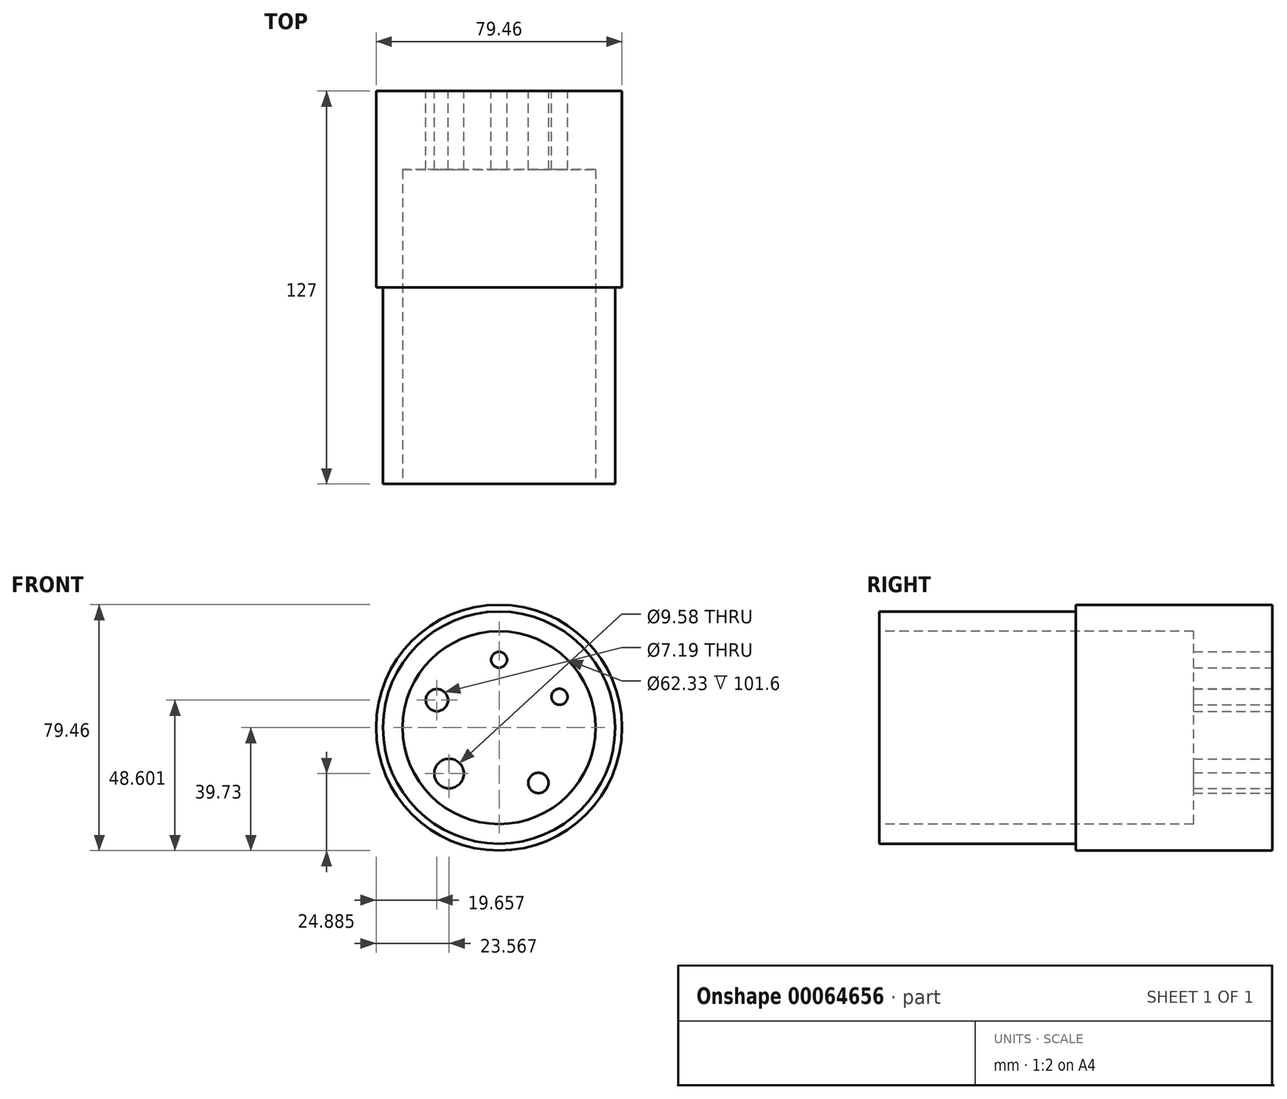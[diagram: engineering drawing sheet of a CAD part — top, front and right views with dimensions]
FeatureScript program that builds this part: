
annotation { "Feature Type Name" : "Feature", "Feature Type Description" : "" }
export const myFeature = defineFeature(function(context is Context, id is Id, definition is map)
    precondition{}
    {
        {
            var Q0;
            Q0=qCreatedBy(makeId("Front.planeOp"),FACE);
            var sketch = newSketch(context, id + "F0", { "sketchPlane" : qUnion([Q0])});
            skCircle(sketch, "E0", {"center": v(0, 0) * mm, "radius": 37.52 * mm});
            skSolve(sketch);
        }
        {
            var Q0;
            Q0=qCreatedBy(makeId("Front.planeOp"),FACE);
            var sketch = newSketch(context, id + "F1", { "sketchPlane" : qUnion([Q0])});
            skCircle(sketch, "E1", {"center": v(0, 0) * mm, "radius": 39.73 * mm});
            skSolve(sketch);
        }
        {
            var Q0;
            Q0=makeQuery(id+"F0.imprint","IMPRINT",FACE,{"disambiguationData":[TD([[makeQuery(id+"F0.imprint","IMPRINT",EDGE,{"derivedFrom":sQuery(id+"F0.wireOp",EDGE,"E0")}),1.0]])]});
            extrude(context, id + "F2", {"entities" : qUnion([Q0]), "depth" : 63.5 * mm});
        }
        {
            var Q0;
            Q0=makeQuery(id+"F1.imprint","IMPRINT",FACE,{"disambiguationData":[TD([[makeQuery(id+"F1.imprint","IMPRINT",EDGE,{"derivedFrom":sQuery(id+"F1.wireOp",EDGE,"E1")}),1.0]])]});
            extrude(context, id + "F3", {"entities" : qUnion([Q0]), "operationType" : NewBodyOperationType.ADD, "oppositeDirection" : true, "depth" : 63.5 * mm});
        }
        {
            var Q0;
            Q0=makeQuery(id+"F3.opExtrude","CAP_FACE",FACE,{"disambiguationData":[OSD([sQuery(id+"F1.wireOp",EDGE,"E1")])],"isStart":false});
            var sketch = newSketch(context, id + "F4", { "sketchPlane" : qUnion([Q0])});
            skCircle(sketch, "E2", {"center": v(0, 21.95) * mm, "radius": 2.57 * mm});
            skCircle(sketch, "E3", {"center": v(-19.55, 9.98) * mm, "radius": 2.6 * mm});
            skCircle(sketch, "E4", {"center": v(20.07, 8.87) * mm, "radius": 3.6 * mm});
            skCircle(sketch, "E5", {"center": v(-12.72, -17.88) * mm, "radius": 3.28 * mm});
            skCircle(sketch, "E6", {"center": v(16.16, -14.85) * mm, "radius": 4.79 * mm});
            skSolve(sketch);
        }
        {
            var Q0;
            Q0 = qSketchRegion(id + "F4", true);
            extrude(context, id + "F5", {"entities" : qUnion([Q0]), "operationType" : NewBodyOperationType.REMOVE, "endBound" : BoundingType.THROUGH_ALL, "oppositeDirection" : true, "depth" : 25.4 * mm});
        }
        {
            var Q0;
            Q0=makeQuery(id+"F2.opExtrude","CAP_FACE",FACE,{"disambiguationData":[OSD([sQuery(id+"F0.wireOp",EDGE,"E0")])],"isStart":false});
            var sketch = newSketch(context, id + "F6", { "sketchPlane" : qUnion([Q0])});
            skCircle(sketch, "E7.0", {"center": v(0, 0) * mm, "radius": 31.17 * mm});
            skSolve(sketch);
        }
        {
            var Q0;
            Q0=makeQuery(id+"F6.imprint","IMPRINT",FACE,{"disambiguationData":[TD([[makeQuery(id+"F6.imprint","IMPRINT",EDGE,{"derivedFrom":sQuery(id+"F6.wireOp",EDGE,"E7.0")}),1.0]])]});
            extrude(context, id + "F7", {"entities" : qUnion([Q0]), "operationType" : NewBodyOperationType.REMOVE, "oppositeDirection" : true, "depth" : 101.6 * mm});
        }
    });
